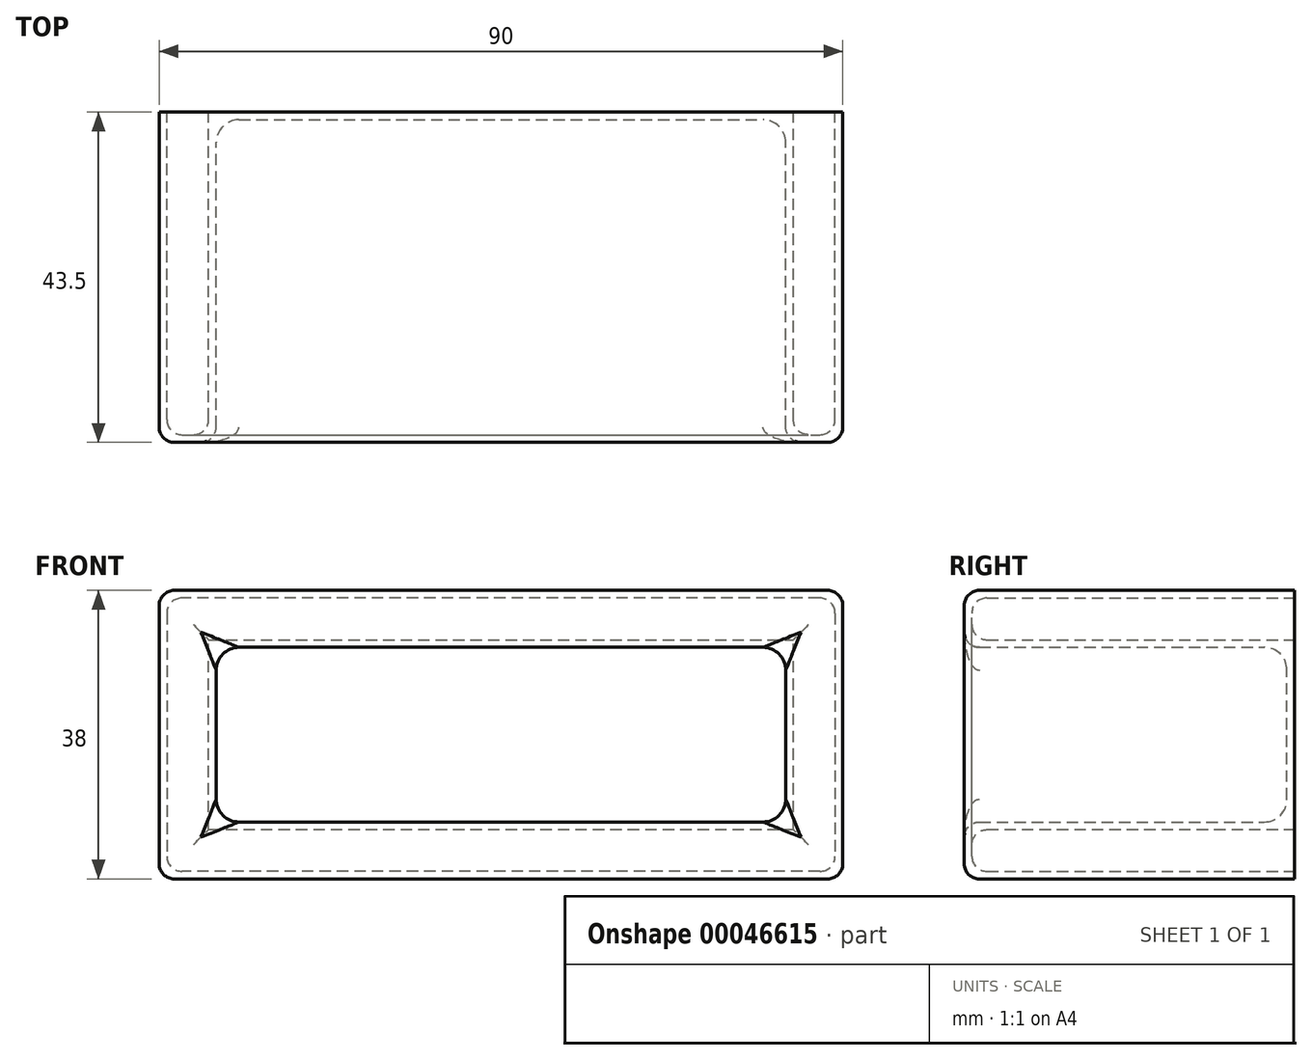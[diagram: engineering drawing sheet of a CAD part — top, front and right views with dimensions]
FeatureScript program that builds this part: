
annotation { "Feature Type Name" : "Feature", "Feature Type Description" : "" }
export const myFeature = defineFeature(function(context is Context, id is Id, definition is map)
    precondition{}
    {
        {
            var Q0;
            Q0=qCreatedBy(makeId("Front.planeOp"),FACE);
            var sketch = newSketch(context, id + "F0", { "sketchPlane" : qUnion([Q0])});
            skLineSegment(sketch, "E0.bottom", {"start": v(0, 0) * mm, "end": v(90, 0) * mm});
            skLineSegment(sketch, "E0.top", {"start": v(0, 38) * mm, "end": v(90, 38) * mm});
            skLineSegment(sketch, "E0.left", {"start": v(0, 0) * mm, "end": v(0, 38) * mm});
            skLineSegment(sketch, "E0.right", {"start": v(90, 0) * mm, "end": v(90, 38) * mm});
            skSolve(sketch);
        }
        {
            var Q0;
            Q0=makeQuery(id+"F0.imprint","IMPRINT",FACE,{"disambiguationData":[TD([[makeQuery(id+"F0.imprint","IMPRINT",EDGE,{"derivedFrom":sQuery(id+"F0.wireOp",EDGE,"E0.bottom")}),1.0]])]});
            extrude(context, id + "F1", {"entities" : qUnion([Q0]), "depth" : 50 * mm});
        }
        {
            var Q0;
            Q0=makeQuery(id+"F1.opExtrude","CAP_FACE",FACE,{"disambiguationData":[OSD([sQuery(id+"F0.wireOp",EDGE,"E0.bottom"),sQuery(id+"F0.wireOp",EDGE,"E0.top"),sQuery(id+"F0.wireOp",EDGE,"E0.left"),sQuery(id+"F0.wireOp",EDGE,"E0.right")])],"isStart":false});
            shell(context, id + "F2", {"entities" : qUnion([Q0]), "thickness" : 7.5 * mm});
        }
        {
            var Q0;
            Q0=makeQuery(id+"F1.opExtrude","CAP_FACE",FACE,{"disambiguationData":[OSD([sQuery(id+"F0.wireOp",EDGE,"E0.bottom"),sQuery(id+"F0.wireOp",EDGE,"E0.top"),sQuery(id+"F0.wireOp",EDGE,"E0.left"),sQuery(id+"F0.wireOp",EDGE,"E0.right")])],"isStart":true});
            shell(context, id + "F3", {"entities" : qUnion([Q0]), "thickness" : 1 * mm});
        }
        {
            var Q0;
            Q0=makeQuery(id+"F1.opExtrude","SWEPT_FACE",FACE,{"disambiguationData":[OSD([sQuery(id+"F0.wireOp",EDGE,"E0.bottom")])]});
            var sketch = newSketch(context, id + "F4", { "sketchPlane" : qUnion([Q0])});
            skLineSegment(sketch, "E1.bottom", {"start": v(0, 0) * mm, "end": v(90, 0) * mm});
            skLineSegment(sketch, "E1.top", {"start": v(0, 6.5) * mm, "end": v(90, 6.5) * mm});
            skLineSegment(sketch, "E1.left", {"start": v(0, 0) * mm, "end": v(0, 6.5) * mm});
            skLineSegment(sketch, "E1.right", {"start": v(90, 0) * mm, "end": v(90, 6.5) * mm});
            skSolve(sketch);
        }
        {
            var Q0;
            Q0=makeQuery(id+"F4.imprint","IMPRINT",FACE,{"disambiguationData":[TD([[makeQuery(id+"F4.imprint","IMPRINT",EDGE,{"derivedFrom":sQuery(id+"F4.wireOp",EDGE,"E1.bottom")}),1.0]])]});
            extrude(context, id + "F5", {"entities" : qUnion([Q0]), "operationType" : NewBodyOperationType.REMOVE, "endBound" : BoundingType.THROUGH_ALL, "oppositeDirection" : true, "depth" : 25 * mm});
        }
        {
            var Q0;
            Q0=makeQuery(id+"F1.opExtrude","CAP_EDGE",EDGE,{"disambiguationData":[OSD([sQuery(id+"F0.wireOp",EDGE,"E0.bottom")])],"isStart":false});
            var Q1;
            Q1=makeQuery(id+"F1.opExtrude","CAP_EDGE",EDGE,{"disambiguationData":[OSD([sQuery(id+"F0.wireOp",EDGE,"E0.right")])],"isStart":false});
            var Q2;
            Q2=makeQuery(id+"F1.opExtrude","CAP_EDGE",EDGE,{"disambiguationData":[OSD([sQuery(id+"F0.wireOp",EDGE,"E0.top")])],"isStart":false});
            var Q3;
            Q3=makeQuery(id+"F1.opExtrude","CAP_FACE",FACE,{"disambiguationData":[OSD([sQuery(id+"F0.wireOp",EDGE,"E0.bottom"),sQuery(id+"F0.wireOp",EDGE,"E0.top"),sQuery(id+"F0.wireOp",EDGE,"E0.left"),sQuery(id+"F0.wireOp",EDGE,"E0.right")])],"isStart":false});
            var Q4;
            {var subQ0=sQuery(id+"F0.wireOp",EDGE,"E0.bottom");var subQ1=sQuery(id+"F0.wireOp",EDGE,"E0.top");var subQ2=sQuery(id+"F0.wireOp",EDGE,"E0.left");var subQ3=sQuery(id+"F0.wireOp",EDGE,"E0.right");Q4=makeQuery(id+"F3.opShell","OFFSET_FACE",FACE,{"disambiguationData":[OSD([subQ0,subQ1,subQ2,subQ3]),TDD([makeQuery(id+"F1.opExtrude","CAP_FACE",FACE,{"disambiguationData":[OSD([subQ0,subQ1,subQ2,subQ3])],"isStart":false})])]});}
            fillet(context, id + "F6", {"entities" : qUnion([Q0, Q1, Q2, Q3, Q4]), "radius" : 2 * mm, "tangentPropagation" : true, "allowEdgeOverflow" : false});
        }
        {
            var Q0;
            Q0=makeQuery(id+"F1.opExtrude","SWEPT_EDGE",EDGE,{"disambiguationData":[OSD([sQuery(id+"F0.wireOp",EDGE,"E0.bottom"),sQuery(id+"F0.wireOp",EDGE,"E0.left")])]});
            var Q1;
            Q1=makeQuery(id+"F1.opExtrude","SWEPT_EDGE",EDGE,{"disambiguationData":[OSD([sQuery(id+"F0.wireOp",EDGE,"E0.top"),sQuery(id+"F0.wireOp",EDGE,"E0.left")])]});
            var Q2;
            Q2=makeQuery(id+"F1.opExtrude","SWEPT_EDGE",EDGE,{"disambiguationData":[OSD([sQuery(id+"F0.wireOp",EDGE,"E0.bottom"),sQuery(id+"F0.wireOp",EDGE,"E0.right")])]});
            var Q3;
            Q3=makeQuery(id+"F1.opExtrude","SWEPT_EDGE",EDGE,{"disambiguationData":[OSD([sQuery(id+"F0.wireOp",EDGE,"E0.top"),sQuery(id+"F0.wireOp",EDGE,"E0.right")])]});
            var Q4;
            {var subQ0=sQuery(id+"F0.wireOp",EDGE,"E0.top");var subQ1=sQuery(id+"F0.wireOp",EDGE,"E0.right");Q4=makeQuery(id+"F3.opShell","OFFSET_EDGE",EDGE,{"disambiguationData":[OSD([subQ0,subQ1]),TDD([makeQuery(id+"F1.opExtrude","SWEPT_EDGE",EDGE,{"disambiguationData":[OSD([subQ0,subQ1])]})])]});}
            var Q5;
            {var subQ0=sQuery(id+"F0.wireOp",EDGE,"E0.bottom");var subQ1=sQuery(id+"F0.wireOp",EDGE,"E0.left");Q5=makeQuery(id+"F3.opShell","OFFSET_EDGE",EDGE,{"disambiguationData":[OSD([subQ0,subQ1]),TDD([makeQuery(id+"F1.opExtrude","SWEPT_EDGE",EDGE,{"disambiguationData":[OSD([subQ0,subQ1])]})])]});}
            var Q6;
            {var subQ0=sQuery(id+"F0.wireOp",EDGE,"E0.top");var subQ1=sQuery(id+"F0.wireOp",EDGE,"E0.left");Q6=makeQuery(id+"F3.opShell","OFFSET_EDGE",EDGE,{"disambiguationData":[OSD([subQ0,subQ1]),TDD([makeQuery(id+"F1.opExtrude","SWEPT_EDGE",EDGE,{"disambiguationData":[OSD([subQ0,subQ1])]})])]});}
            var Q7;
            {var subQ0=sQuery(id+"F0.wireOp",EDGE,"E0.bottom");var subQ1=sQuery(id+"F0.wireOp",EDGE,"E0.right");Q7=makeQuery(id+"F3.opShell","OFFSET_EDGE",EDGE,{"disambiguationData":[OSD([subQ0,subQ1]),TDD([makeQuery(id+"F1.opExtrude","SWEPT_EDGE",EDGE,{"disambiguationData":[OSD([subQ0,subQ1])]})])]});}
            fillet(context, id + "F7", {"entities" : qUnion([Q0, Q1, Q2, Q3, Q4, Q5, Q6, Q7]), "radius" : 2 * mm, "tangentPropagation" : true, "allowEdgeOverflow" : false});
        }
        {
            var Q0;
            Q0=makeQuery(id+"F2.opShell","OFFSET_FACE",FACE,{"disambiguationData":[OSD([sQuery(id+"F0.wireOp",EDGE,"E0.bottom"),sQuery(id+"F0.wireOp",EDGE,"E0.top"),sQuery(id+"F0.wireOp",EDGE,"E0.left"),sQuery(id+"F0.wireOp",EDGE,"E0.right")])]});
            var Q1;
            Q1=makeQuery(id+"F2.opShell","OFFSET_FACE",FACE,{"disambiguationData":[OSD([sQuery(id+"F0.wireOp",EDGE,"E0.right")])]});
            var Q2;
            Q2=makeQuery(id+"F2.opShell","OFFSET_FACE",FACE,{"disambiguationData":[OSD([sQuery(id+"F0.wireOp",EDGE,"E0.left")])]});
            fillet(context, id + "F8", {"entities" : qUnion([Q0, Q1, Q2]), "radius" : 3 * mm, "tangentPropagation" : true, "allowEdgeOverflow" : false});
        }
    });
